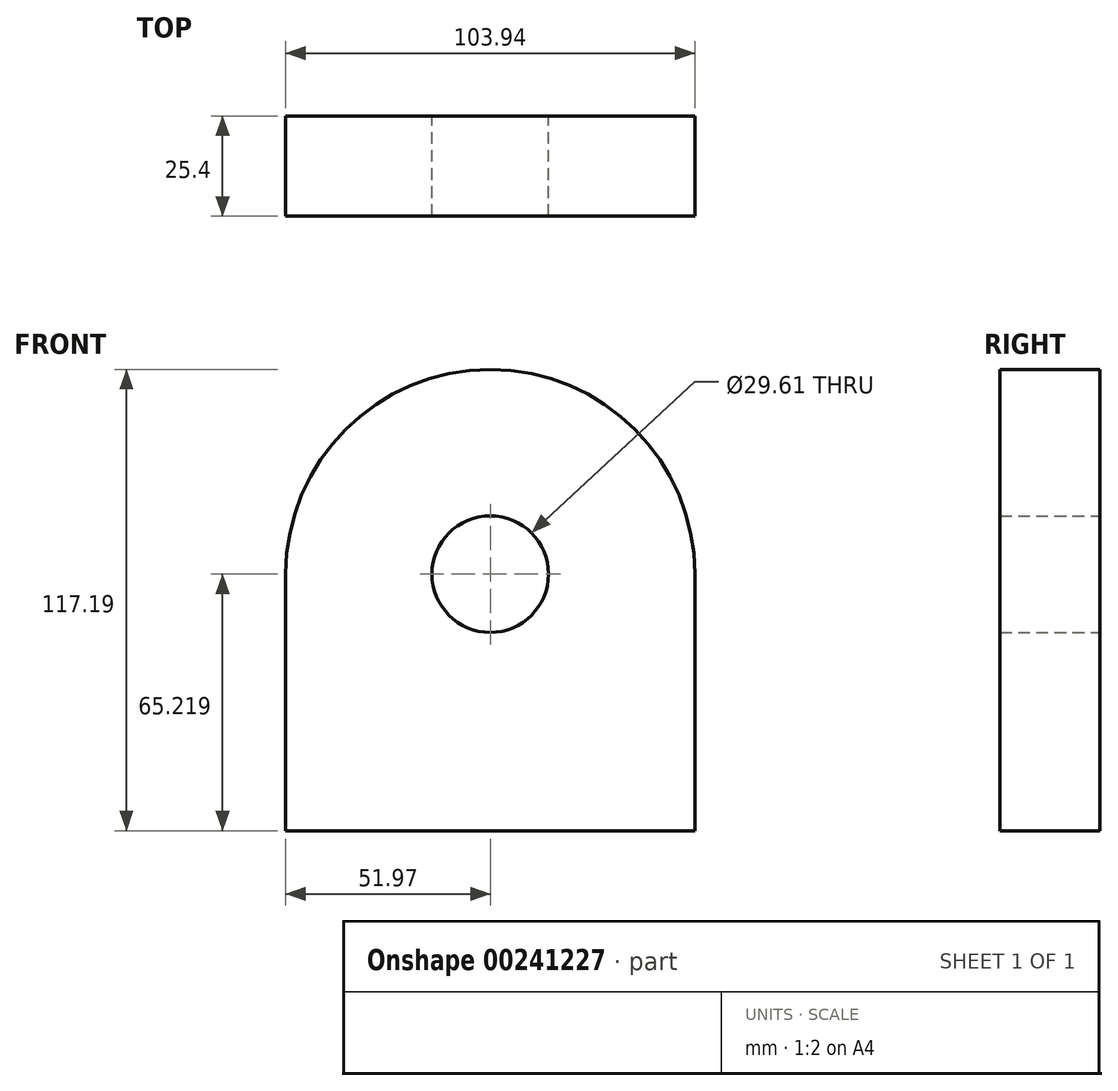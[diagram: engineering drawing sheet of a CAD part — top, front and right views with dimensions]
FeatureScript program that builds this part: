
annotation { "Feature Type Name" : "Feature", "Feature Type Description" : "" }
export const myFeature = defineFeature(function(context is Context, id is Id, definition is map)
    precondition{}
    {
        {
            var Q0;
            Q0=qCreatedBy(makeId("Front.planeOp"),FACE);
            var sketch = newSketch(context, id + "F0", { "sketchPlane" : qUnion([Q0])});
            skLineSegment(sketch, "E0.bottom", {"start": v(51.97, -32.6) * mm, "end": v(-51.97, -32.6) * mm});
            skLineSegment(sketch, "E0.top", {"start": v(51.97, 32.6) * mm, "end": v(28.86, 32.6) * mm});
            skLineSegment(sketch, "E0.left", {"start": v(51.97, -32.6) * mm, "end": v(51.97, 32.6) * mm});
            skLineSegment(sketch, "E0.right", {"start": v(-51.97, -32.6) * mm, "end": v(-51.97, 32.6) * mm});
            skPoint(sketch, "E0.middle", {"position": v(0, 0) * mm});
            skCircle(sketch, "E1", {"center": v(0, 32.6) * mm, "radius": 28.86 * mm});
            skCircle(sketch, "E2", {"center": v(0, 32.6) * mm, "radius": 14.8 * mm});
            skArc(sketch, "E3", {"start": v(51.97, 32.6) * mm, "mid": v(0, 84.58) * mm, "end": v(-51.97, 32.6) * mm});
            skLineSegment(sketch, "E4.trimOffspring", {"start": v(-28.86, 32.6) * mm, "end": v(-51.97, 32.6) * mm});
            skSolve(sketch);
        }
        {
            var Q0;
            Q0=makeQuery(id+"F0.imprint","IMPRINT",FACE,{"disambiguationData":[TD([[makeQuery(id+"F0.imprint","IMPRINT",EDGE,{"derivedFrom":sQuery(id+"F0.wireOp",EDGE,"E2")}),-1.0]])]});
            var Q1;
            Q1=makeQuery(id+"F0.imprint","IMPRINT",FACE,{"disambiguationData":[TD([[makeQuery(id+"F0.imprint","IMPRINT",EDGE,{"derivedFrom":sQuery(id+"F0.wireOp",EDGE,"E0.bottom")}),-1.0]])]});
            var Q2;
            {var subQ0=sQuery(id+"F0.wireOp",EDGE,"E0.top");Q2=makeQuery(id+"F0.imprint","IMPRINT",FACE,{"disambiguationData":[TD([[makeQuery(id+"F0.imprint","IMPRINT",EDGE,{"derivedFrom":subQ0}),-1.0]])]});}
            extrude(context, id + "F1", {"entities" : qUnion([Q0, Q1, Q2]), "depth" : 25.4 * mm});
        }
    });
